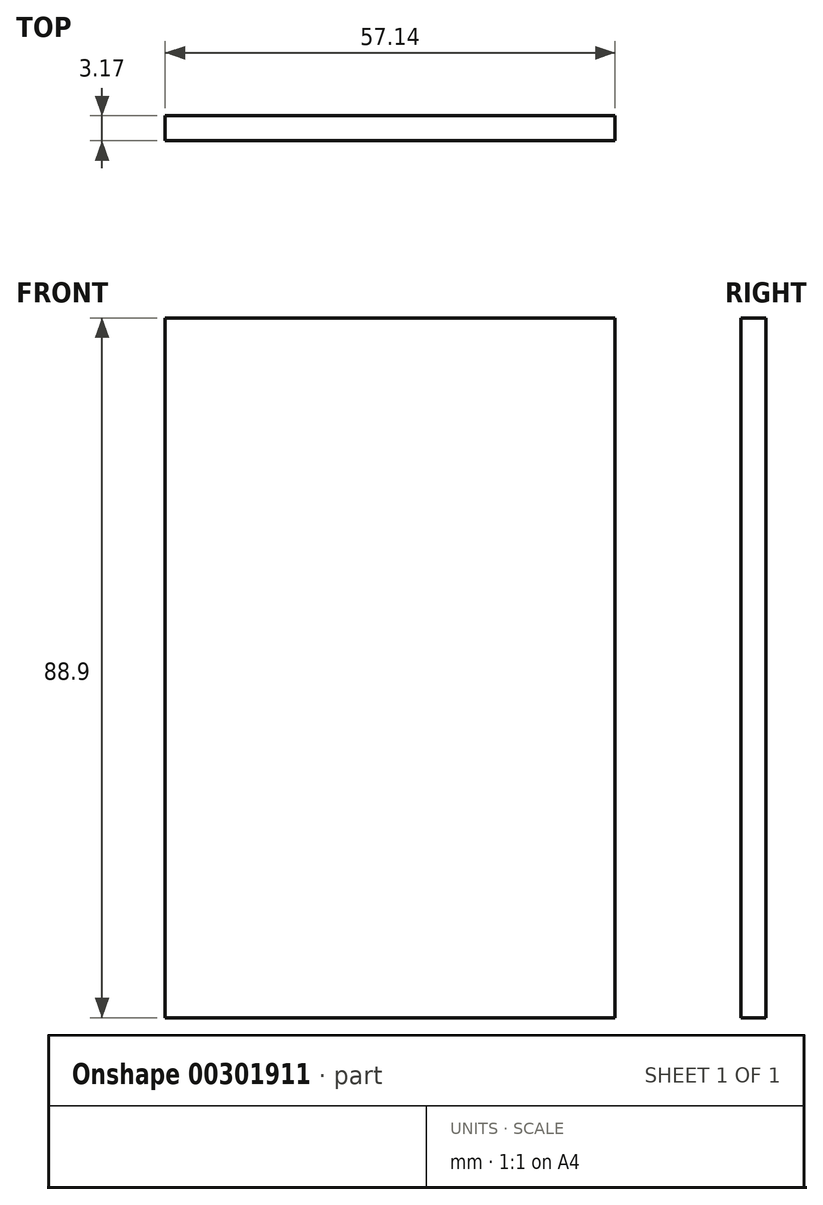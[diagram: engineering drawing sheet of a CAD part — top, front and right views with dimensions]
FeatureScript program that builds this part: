
annotation { "Feature Type Name" : "Feature", "Feature Type Description" : "" }
export const myFeature = defineFeature(function(context is Context, id is Id, definition is map)
    precondition{}
    {
        {
            var Q0;
            Q0=qCreatedBy(makeId("Front.planeOp"),FACE);
            var sketch = newSketch(context, id + "F0", { "sketchPlane" : qUnion([Q0])});
            skLineSegment(sketch, "E0.bottom", {"start": v(28.58, 44.45) * mm, "end": v(-28.57, 44.45) * mm});
            skLineSegment(sketch, "E0.top", {"start": v(28.58, -44.45) * mm, "end": v(-28.58, -44.45) * mm});
            skLineSegment(sketch, "E0.left", {"start": v(28.58, 44.45) * mm, "end": v(28.58, -44.45) * mm});
            skLineSegment(sketch, "E0.right", {"start": v(-28.58, 44.45) * mm, "end": v(-28.58, -44.45) * mm});
            skPoint(sketch, "E0.middle", {"position": v(0, 0) * mm});
            skSolve(sketch);
        }
        {
            var Q0;
            Q0=makeQuery(id+"F0.imprint","IMPRINT",FACE,{"disambiguationData":[TD([[makeQuery(id+"F0.imprint","IMPRINT",EDGE,{"derivedFrom":sQuery(id+"F0.wireOp",EDGE,"E0.bottom")}),1.0]])]});
            extrude(context, id + "F1", {"entities" : qUnion([Q0]), "depth" : 3.17 * mm});
        }
    });
